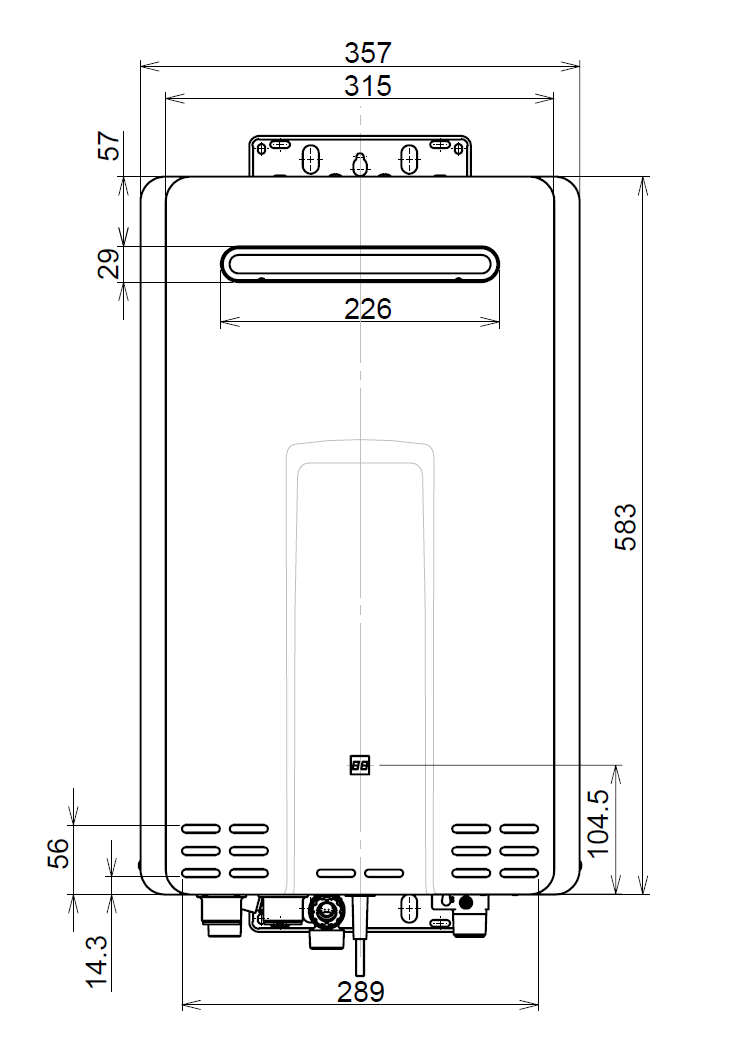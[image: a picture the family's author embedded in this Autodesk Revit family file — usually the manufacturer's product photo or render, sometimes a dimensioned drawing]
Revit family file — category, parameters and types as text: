
# Revit family: hd49e  wirh pipe cover(2)
name_source: partatom
category: Generic Models
units: mm (PartAtom-declared; Revit-internal decimal feet)

## family parameters
Can host rebar = No
Cut with Voids When Loaded = No
Host = Face
Part Type = Normal
Room Calculation Point = No
Round Connector Dimension = Use Diameter
Shared = No

## types (2) — shared parameters
Cold connection from back of unit = 46 mm
Cold connection from centreline = 27 mm
Cold water connection = 20 mm
Cold water inlet = R¾ (20 mm)
Default Elevation = 1219 mm
Efficiency = 82%
Gas connection = 20 mm
Gas connection from back of unit = 75 mm  [stored 0.246063 ft]
Gas connection from centreline = 89 mm
Gas supply = R¾ (20 mm)
Hot connection from back of unit = 67 mm
Hot connection from centreline = 110 mm
Hot water capacity = 1.4-37 L/min
Hot water connection = 20 mm
Hot water outlet = R¾ (20 mm)
Ignition system = Direct electronic ignition
Ingress protection rating = IPX5
Input = 11-210 MJ/h
Installation = This appliance is designed for outdoor installation only. It MUST BE located above ground in open air with natural ventilation, without stagnant areas, where gas leakage and products of combustion can be rapidly dispersed by wind and natural convection.
Line pressure maximum = 3.5 kPa (maximum standing pressure under abnormal intermittent conditions is 5.0 kPa).
In the case of commercial metering (i.e. 35-37 kPa coming in), there may be a requirement to regulate the incoming line pressure down
Manufacturer = Rinnai
Minimum water flow = 1.5 L/min
NOx af = 40ppm
Noise level = 52
Nominal operating pressure (water supply) = 200-1000kPa
Nominal water capacity = 28 L/min @25° rise (1680L/h)
Output = 48.8 kW
Power consumption (antifrost) = 120 W
Power consumption (normal) = 95 W
Power consumption (standby) = 2 W
Type Comments = HD49 units are primarily designed for commercial applications, but can be used for larger hot water capacity residential projects.
Weight = 20 kg

## per-type parameters (varying)
| type | Constraint | Description | Line pressure | Model |
| HD49e (NG) | 1 | HD49 External Natural Gas | 1.13-3.0 kPa | HD49eN |
| HD49e (LPG) | 2 | HD49 External LPG | 2.75-3.0 kPa | HD49eL |

note: [stored X ft] marks values corroborated as IEEE doubles in the binary element streams (Revit-internal decimal feet)

## geometry (parser evidence)
native form markers: Sweep x2
no freeform markers — native parametric forms only
